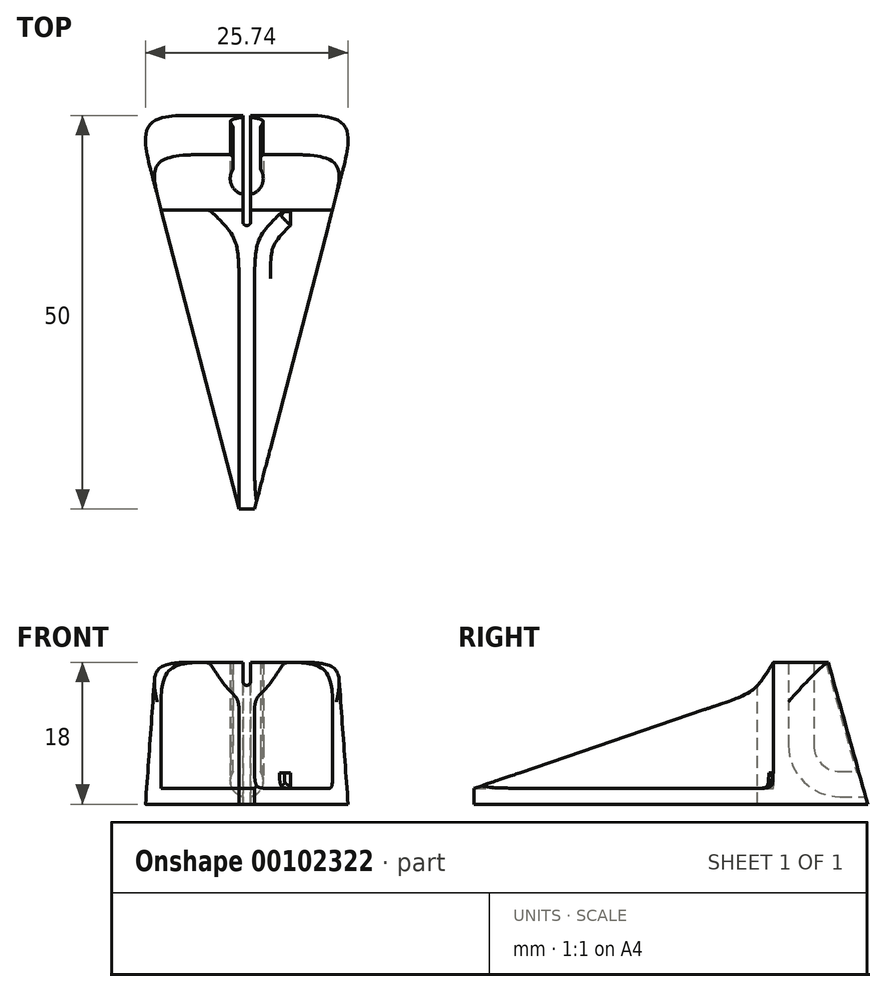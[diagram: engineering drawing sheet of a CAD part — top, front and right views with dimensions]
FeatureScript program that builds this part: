
annotation { "Feature Type Name" : "Feature", "Feature Type Description" : "" }
export const myFeature = defineFeature(function(context is Context, id is Id, definition is map)
    precondition{}
    {
        {
            var Q0;
            Q0=qCreatedBy(makeId("Top.planeOp"),FACE);
            var sketch = newSketch(context, id + "F0", { "sketchPlane" : qUnion([Q0])});
            skLineSegment(sketch, "E0", {"start": v(0, 0) * mm, "end": v(0, -42) * mm});
            skLineSegment(sketch, "E1", {"start": v(0, -42) * mm, "end": v(1, -42) * mm});
            skLineSegment(sketch, "E2", {"start": v(1, -42) * mm, "end": v(14, 8) * mm});
            skLineSegment(sketch, "E3", {"start": v(14, 8) * mm, "end": v(2, 8) * mm});
            skLineSegment(sketch, "E4", {"start": v(2, 8) * mm, "end": v(2, 0) * mm, "construction": true});
            skLineSegment(sketch, "E5", {"start": v(2, 0) * mm, "end": v(0, 0) * mm, "construction": true});
            skLineSegment(sketch, "E6", {"start": v(0, 0) * mm, "end": v(0, 8) * mm});
            skLineSegment(sketch, "E7", {"start": v(0, 8) * mm, "end": v(2, 8) * mm});
            skSolve(sketch);
        }
        {
            var Q0;
            Q0 = qSketchRegion(id + "F0", true);
            extrude(context, id + "F1", {"entities" : qUnion([Q0]), "depth" : 2 * mm});
        }
        {
            var Q0;
            Q0=makeQuery(id+"F1.opExtrude","SWEPT_BODY",BODY,{"disambiguationData":[OSD([sQuery(id+"F0.wireOp",EDGE,"E0"),sQuery(id+"F0.wireOp",EDGE,"E1"),sQuery(id+"F0.wireOp",EDGE,"E2"),sQuery(id+"F0.wireOp",EDGE,"E3"),sQuery(id+"F0.wireOp",EDGE,"E4"),sQuery(id+"F0.wireOp",EDGE,"E5")])]});
            var Q1;
            Q1=makeQuery(id+"F1.opExtrude","SWEPT_FACE",FACE,{"disambiguationData":[OSD([sQuery(id+"F0.wireOp",EDGE,"E0")])]});
            mirror(context, id + "F2", {"operationType" : NewBodyOperationType.ADD, "entities" : qUnion([Q0]), "mirrorPlane" : qUnion([Q1])});
        }
        {
            var Q0;
            {var subQ0=makeQuery(id+"F1.opExtrude","CAP_FACE",FACE,{"disambiguationData":[OSD([sQuery(id+"F0.wireOp",EDGE,"E0"),sQuery(id+"F0.wireOp",EDGE,"E1"),sQuery(id+"F0.wireOp",EDGE,"E2"),sQuery(id+"F0.wireOp",EDGE,"E3"),sQuery(id+"F0.wireOp",EDGE,"E6"),sQuery(id+"F0.wireOp",EDGE,"E7")])],"isStart":false});Q0=makeQuery(id+"F2.boolean.opBoolean","MERGE",FACE,{"derivedFrom":[subQ0,makeQuery(id+"F2.opPattern","COPY",FACE,{"derivedFrom":subQ0,"instanceName":"1"})]});}
            var sketch = newSketch(context, id + "F3", { "sketchPlane" : qUnion([Q0])});
            skLineSegment(sketch, "E8", {"start": v(0, 0) * mm, "end": v(1.75, 0) * mm});
            skLineSegment(sketch, "E9", {"start": v(1.75, 0) * mm, "end": v(1.75, 8) * mm});
            skLineSegment(sketch, "E10", {"start": v(1.75, 8) * mm, "end": v(4.75, 8) * mm});
            skLineSegment(sketch, "E11", {"start": v(-1, -6.17) * mm, "end": v(-4.75, -4) * mm});
            skLineSegment(sketch, "E12", {"start": v(-4.75, 8) * mm, "end": v(-1.75, 8) * mm});
            skLineSegment(sketch, "E13", {"start": v(-1.75, 8) * mm, "end": v(-1.75, 0) * mm});
            skLineSegment(sketch, "E14", {"start": v(-1.75, 0) * mm, "end": v(0, 0) * mm});
            skLineSegment(sketch, "E15", {"start": v(-4.75, -4) * mm, "end": v(4.75, -4) * mm, "construction": true});
            skLineSegment(sketch, "E16", {"start": v(-1, -6.17) * mm, "end": v(-1, -42) * mm});
            skLineSegment(sketch, "E17", {"start": v(-1, -42) * mm, "end": v(1, -42) * mm});
            skLineSegment(sketch, "E18", {"start": v(1, -42) * mm, "end": v(1, -6.17) * mm});
            skLineSegment(sketch, "E19", {"start": v(1, -6.17) * mm, "end": v(4.75, -4) * mm});
            skLineSegment(sketch, "E20", {"start": v(-4.75, -4) * mm, "end": v(-10.88, -4) * mm});
            skLineSegment(sketch, "E21", {"start": v(-10.88, -4) * mm, "end": v(-11.66, -1) * mm});
            skLineSegment(sketch, "E22", {"start": v(-11.66, -1) * mm, "end": v(-4.75, -1) * mm, "construction": true});
            skLineSegment(sketch, "E23", {"start": v(-4.75, -1) * mm, "end": v(-4.75, 8) * mm, "construction": true});
            skLineSegment(sketch, "E24", {"start": v(4.75, 8) * mm, "end": v(4.75, -1) * mm, "construction": true});
            skLineSegment(sketch, "E25", {"start": v(4.75, -1) * mm, "end": v(11.66, -1) * mm, "construction": true});
            skLineSegment(sketch, "E26", {"start": v(11.66, -1) * mm, "end": v(10.88, -4) * mm});
            skLineSegment(sketch, "E27", {"start": v(10.88, -4) * mm, "end": v(4.75, -4) * mm});
            skLineSegment(sketch, "E28", {"start": v(4.75, -1) * mm, "end": v(4.75, -4) * mm, "construction": true});
            skLineSegment(sketch, "E29", {"start": v(-4.75, -1) * mm, "end": v(-4.75, -4) * mm, "construction": true});
            skLineSegment(sketch, "E30", {"start": v(4.75, 8) * mm, "end": v(14, 8) * mm});
            skLineSegment(sketch, "E31", {"start": v(14, 8) * mm, "end": v(11.66, -1) * mm});
            skLineSegment(sketch, "E32", {"start": v(-4.75, 8) * mm, "end": v(-14, 8) * mm});
            skLineSegment(sketch, "E33", {"start": v(-14, 8) * mm, "end": v(-11.66, -1) * mm});
            skSolve(sketch);
        }
        {
            var Q0;
            Q0 = qSketchRegion(id + "F3", true);
            extrude(context, id + "F4", {"entities" : qUnion([Q0]), "operationType" : NewBodyOperationType.ADD, "depth" : 16 * mm});
        }
        {
            var Q0;
            Q0=qCreatedBy(makeId("Right.planeOp"),FACE);
            var sketch = newSketch(context, id + "F5", { "sketchPlane" : qUnion([Q0])});
            skLineSegment(sketch, "E34", {"start": v(8, 18) * mm, "end": v(8, 0) * mm});
            skLineSegment(sketch, "E35", {"start": v(8, 0) * mm, "end": v(3, 18) * mm});
            skLineSegment(sketch, "E36", {"start": v(3, 18) * mm, "end": v(8, 18) * mm});
            skSolve(sketch);
        }
        {
            var Q0;
            Q0 = qSketchRegion(id + "F5", true);
            extrude(context, id + "F6", {"entities" : qUnion([Q0]), "operationType" : NewBodyOperationType.REMOVE, "endBound" : BoundingType.THROUGH_ALL, "oppositeDirection" : true, "depth" : 25 * mm, "hasSecondDirection" : true, "secondDirectionBound" : SecondDirectionBoundingType.THROUGH_ALL, "secondDirectionOppositeDirection" : false, "secondDirectionDepth" : 25 * mm});
        }
        {
            var Q0;
            Q0=qCreatedBy(makeId("Right.planeOp"),FACE);
            var sketch = newSketch(context, id + "F7", { "sketchPlane" : qUnion([Q0])});
            skLineSegment(sketch, "E37", {"start": v(-4, 18) * mm, "end": v(-6.17, 14.25) * mm});
            skLineSegment(sketch, "E38", {"start": v(-6.17, 14.25) * mm, "end": v(-42, 2) * mm});
            skLineSegment(sketch, "E39", {"start": v(-42, 2) * mm, "end": v(-42, 18) * mm});
            skLineSegment(sketch, "E40", {"start": v(-42, 18) * mm, "end": v(-4, 18) * mm});
            skSolve(sketch);
        }
        {
            var Q0;
            Q0 = qSketchRegion(id + "F7", true);
            extrude(context, id + "F8", {"entities" : qUnion([Q0]), "operationType" : NewBodyOperationType.REMOVE, "endBound" : BoundingType.THROUGH_ALL, "oppositeDirection" : true, "depth" : 25 * mm, "hasSecondDirection" : true, "secondDirectionBound" : SecondDirectionBoundingType.THROUGH_ALL, "secondDirectionOppositeDirection" : false, "secondDirectionDepth" : 25 * mm});
        }
        {
            var Q0;
            Q0=makeQuery(id+"F4.opExtrude","SWEPT_EDGE",EDGE,{"disambiguationData":[OSD([sQuery(id+"F3.wireOp",EDGE,"E11"),sQuery(id+"F3.wireOp",EDGE,"E16")])]});
            var Q1;
            Q1=makeQuery(id+"F8.boolean.opBoolean","COPY",EDGE,{"derivedFrom":makeQuery(id+"F8.opExtrude","SWEPT_EDGE",EDGE,{"disambiguationData":[OSD([sQuery(id+"F7.wireOp",EDGE,"E37"),sQuery(id+"F7.wireOp",EDGE,"E38")])]})});
            var Q2;
            Q2=makeQuery(id+"F4.opExtrude","SWEPT_EDGE",EDGE,{"disambiguationData":[OSD([sQuery(id+"F3.wireOp",EDGE,"E18"),sQuery(id+"F3.wireOp",EDGE,"E19")])]});
            fillet(context, id + "F9", {"entities" : qUnion([Q0, Q1, Q2]), "radius" : 12 * mm, "tangentPropagation" : true, "rho" : 0.7, "crossSection" : FilletCrossSection.CONIC, "allowEdgeOverflow" : false});
        }
        {
            var Q0;
            Q0=makeQuery(id+"F4.opExtrude","CAP_EDGE",EDGE,{"disambiguationData":[OSD([sQuery(id+"F3.wireOp",EDGE,"E18")])],"isStart":true});
            var Q1;
            Q1=makeQuery(id+"F4.opExtrude","CAP_EDGE",EDGE,{"disambiguationData":[OSD([sQuery(id+"F3.wireOp",EDGE,"E16")])],"isStart":true});
            var Q2;
            Q2=makeQuery(id+"F9.opFillet","BLEND_EDGE",EDGE,{"blendedFrom":[makeQuery(id+"F4.opExtrude","SWEPT_EDGE",EDGE,{"disambiguationData":[OSD([sQuery(id+"F3.wireOp",EDGE,"E11"),sQuery(id+"F3.wireOp",EDGE,"E16")])]}),makeQuery(id+"F4.opExtrude","SWEPT_FACE",FACE,{"disambiguationData":[OSD([sQuery(id+"F3.wireOp",EDGE,"E20")])]})],"blendedInto":[makeQuery(id+"F4.opExtrude","SWEPT_FACE",FACE,{"disambiguationData":[OSD([sQuery(id+"F3.wireOp",EDGE,"E20")])]})]});
            var Q3;
            Q3=makeQuery(id+"F9.opFillet","BLEND_EDGE",EDGE,{"blendedFrom":[makeQuery(id+"F4.opExtrude","SWEPT_EDGE",EDGE,{"disambiguationData":[OSD([sQuery(id+"F3.wireOp",EDGE,"E18"),sQuery(id+"F3.wireOp",EDGE,"E19")])]}),makeQuery(id+"F4.opExtrude","SWEPT_FACE",FACE,{"disambiguationData":[OSD([sQuery(id+"F3.wireOp",EDGE,"E27")])]})],"blendedInto":[makeQuery(id+"F4.opExtrude","SWEPT_FACE",FACE,{"disambiguationData":[OSD([sQuery(id+"F3.wireOp",EDGE,"E27")])]})]});
            var Q4;
            Q4=makeQuery(id+"F4.opExtrude","SWEPT_EDGE",EDGE,{"disambiguationData":[OSD([sQuery(id+"F3.wireOp",EDGE,"E24"),sQuery(id+"F3.wireOp",EDGE,"E25")])]});
            var Q5;
            Q5=makeQuery(id+"F4.opExtrude","CAP_EDGE",EDGE,{"disambiguationData":[OSD([sQuery(id+"F3.wireOp",EDGE,"E24")])],"isStart":true});
            var Q6;
            Q6=makeQuery(id+"F4.opExtrude","CAP_EDGE",EDGE,{"disambiguationData":[OSD([sQuery(id+"F3.wireOp",EDGE,"E23")])],"isStart":true});
            var Q7;
            Q7=makeQuery(id+"F4.opExtrude","SWEPT_EDGE",EDGE,{"disambiguationData":[OSD([sQuery(id+"F3.wireOp",EDGE,"E22"),sQuery(id+"F3.wireOp",EDGE,"E23")])]});
            var Q8;
            Q8=makeQuery(id+"F4.opExtrude","CAP_EDGE",EDGE,{"disambiguationData":[OSD([sQuery(id+"F3.wireOp",EDGE,"E20")])],"isStart":true});
            var Q9;
            Q9=makeQuery(id+"F4.opExtrude","CAP_EDGE",EDGE,{"disambiguationData":[OSD([sQuery(id+"F3.wireOp",EDGE,"E27")])],"isStart":true});
            fillet(context, id + "F10", {"entities" : qUnion([Q0, Q1, Q2, Q3, Q4, Q5, Q6, Q7, Q8, Q9]), "radius" : 2 * mm, "tangentPropagation" : true, "rho" : .7, "crossSection" : FilletCrossSection.CONIC, "allowEdgeOverflow" : false});
        }
        {
            var Q0;
            Q0=makeQuery(id+"F6.boolean.opBoolean","INTERSECT",EDGE,{"derivedFrom":[makeQuery(id+"F2.opPattern","COPY",FACE,{"derivedFrom":makeQuery(id+"F1.opExtrude","SWEPT_FACE",FACE,{"disambiguationData":[OSD([sQuery(id+"F0.wireOp",EDGE,"E2")])]}),"instanceName":"1"}),makeQuery(id+"F6.opExtrude","SWEPT_FACE",FACE,{"disambiguationData":[OSD([sQuery(id+"F5.wireOp",EDGE,"E35")])]})]});
            var Q1;
            Q1=makeQuery(id+"F6.boolean.opBoolean","INTERSECT",EDGE,{"derivedFrom":[makeQuery(id+"F1.opExtrude","SWEPT_FACE",FACE,{"disambiguationData":[OSD([sQuery(id+"F0.wireOp",EDGE,"E2")])]}),makeQuery(id+"F6.opExtrude","SWEPT_FACE",FACE,{"disambiguationData":[OSD([sQuery(id+"F5.wireOp",EDGE,"E35")])]})]});
            var Q2;
            Q2=makeQuery(id+"F4.opExtrude","CAP_EDGE",EDGE,{"disambiguationData":[OSD([sQuery(id+"F3.wireOp",EDGE,"E26")])],"isStart":false});
            var Q3;
            Q3=makeQuery(id+"F4.opExtrude","CAP_EDGE",EDGE,{"disambiguationData":[OSD([sQuery(id+"F3.wireOp",EDGE,"E21")])],"isStart":false});
            fillet(context, id + "F11", {"entities" : qUnion([Q0, Q1, Q2, Q3]), "radius" : 5 * mm, "tangentPropagation" : true, "rho" : .6, "crossSection" : FilletCrossSection.CONIC, "allowEdgeOverflow" : false});
        }
        {
            var Q0;
            Q0=qCreatedBy(makeId("Front.planeOp"),FACE);
            var sketch = newSketch(context, id + "F12", { "sketchPlane" : qUnion([Q0])});
            skCircle(sketch, "E41", {"center": v(0, 2.97) * mm, "radius": 2 * mm});
            skSolve(sketch);
        }
        {
            var Q0;
            Q0=qCreatedBy(makeId("Right.planeOp"),FACE);
            var sketch = newSketch(context, id + "F13", { "sketchPlane" : qUnion([Q0])});
            skLineSegment(sketch, "E42", {"start": v(9.7, 2.97) * mm, "end": v(4.5, 2.97) * mm});
            skLineSegment(sketch, "E43", {"start": v(0, 7.47) * mm, "end": v(0, 18) * mm});
            skPoint(sketch, "E44.visualSharp", {"position": v(0, 2.97) * mm});
            skArc(sketch, "E44.filletArc", {"start": v(0, 7.47) * mm, "mid": v(1.32, 4.29) * mm, "end": v(4.5, 2.97) * mm});
            skSolve(sketch);
        }
        {
            var Q0;
            Q0=makeQuery(id+"F4.opExtrude","CAP_FACE",FACE,{"disambiguationData":[OSD([sQuery(id+"F3.wireOp",EDGE,"E8"),sQuery(id+"F3.wireOp",EDGE,"E9"),sQuery(id+"F3.wireOp",EDGE,"E10"),sQuery(id+"F3.wireOp",EDGE,"5PolXJmB-3XB9-REXe-LaWg-8huEXrEMtkN5"),sQuery(id+"F3.wireOp",EDGE,"E11"),sQuery(id+"F3.wireOp",EDGE,"3jHEL8MU-E7O7-Db6z-O08p-L8hBiCzpWRcO"),sQuery(id+"F3.wireOp",EDGE,"E12"),sQuery(id+"F3.wireOp",EDGE,"E13"),sQuery(id+"F3.wireOp",EDGE,"E14"),sQuery(id+"F3.wireOp",EDGE,"E16"),sQuery(id+"F3.wireOp",EDGE,"E17"),sQuery(id+"F3.wireOp",EDGE,"E18"),sQuery(id+"F3.wireOp",EDGE,"E19")])],"isStart":false});
            var sketch = newSketch(context, id + "F14", { "sketchPlane" : qUnion([Q0])});
            skCircle(sketch, "E45", {"center": v(0, 0) * mm, "radius": 2.1 * mm});
            skSolve(sketch);
        }
        {
            var Q0;
            Q0=makeQuery(id+"F4.opExtrude","CAP_EDGE",EDGE,{"disambiguationData":[OSD([sQuery(id+"F3.wireOp",EDGE,"E8"),sQuery(id+"F3.wireOp",EDGE,"E14")])],"isStart":true});
            chamfer(context, id + "F15", {"entities" : qUnion([Q0]), "width" : 4 * mm, "tangentPropagation" : true});
        }
        {
            var Q0;
            Q0 = qSketchRegion(id + "F14", true);
            var Q1;
            Q1 = qConstructionFilter(qBodyType(qCreatedBy(id + "F13" ,EDGE), BodyType.WIRE), ConstructionObject.NO);
            sweep(context, id + "F16", {"operationType" : NewBodyOperationType.REMOVE, "profiles" : qUnion([Q0]), "path" : qUnion([Q1])});
        }
        {
            var Q0;
            Q0=makeQuery(id+"F4.opExtrude","CAP_FACE",FACE,{"disambiguationData":[OSD([sQuery(id+"F3.wireOp",EDGE,"E8"),sQuery(id+"F3.wireOp",EDGE,"E9"),sQuery(id+"F3.wireOp",EDGE,"E10"),sQuery(id+"F3.wireOp",EDGE,"5PolXJmB-3XB9-REXe-LaWg-8huEXrEMtkN5"),sQuery(id+"F3.wireOp",EDGE,"E11"),sQuery(id+"F3.wireOp",EDGE,"3jHEL8MU-E7O7-Db6z-O08p-L8hBiCzpWRcO"),sQuery(id+"F3.wireOp",EDGE,"E12"),sQuery(id+"F3.wireOp",EDGE,"E13"),sQuery(id+"F3.wireOp",EDGE,"E14"),sQuery(id+"F3.wireOp",EDGE,"E16"),sQuery(id+"F3.wireOp",EDGE,"E17"),sQuery(id+"F3.wireOp",EDGE,"E18"),sQuery(id+"F3.wireOp",EDGE,"E19")])],"isStart":false});
            var sketch = newSketch(context, id + "F17", { "sketchPlane" : qUnion([Q0])});
            skLineSegment(sketch, "E46.bottom", {"start": v(-0.5, -6) * mm, "end": v(0.5, -6) * mm});
            skLineSegment(sketch, "E46.top", {"start": v(-0.5, 8) * mm, "end": v(0.5, 8) * mm});
            skLineSegment(sketch, "E46.left", {"start": v(-0.5, -6) * mm, "end": v(-0.5, 8) * mm});
            skLineSegment(sketch, "E46.right", {"start": v(0.5, -6) * mm, "end": v(0.5, 8) * mm});
            skLineSegment(sketch, "E47", {"start": v(0, -6) * mm, "end": v(0, 0) * mm, "construction": true});
            skLineSegment(sketch, "E48", {"start": v(0, -4) * mm, "end": v(0, -6) * mm, "construction": true});
            skSolve(sketch);
        }
        {
            var Q0;
            Q0 = qSketchRegion(id + "F17", true);
            extrude(context, id + "F18", {"entities" : qUnion([Q0]), "operationType" : NewBodyOperationType.REMOVE, "endBound" : BoundingType.THROUGH_ALL, "oppositeDirection" : true, "depth" : 25 * mm});
        }
        {
            var Q0;
            Q0=makeQuery(id+"F18.boolean.opBoolean","COPY",EDGE,{"derivedFrom":makeQuery(id+"F18.opExtrude","SWEPT_EDGE",EDGE,{"disambiguationData":[OSD([sQuery(id+"F17.wireOp",EDGE,"E46.bottom"),sQuery(id+"F17.wireOp",EDGE,"E46.left")])]})});
            var Q1;
            Q1=makeQuery(id+"F18.boolean.opBoolean","COPY",EDGE,{"derivedFrom":makeQuery(id+"F18.opExtrude","SWEPT_EDGE",EDGE,{"disambiguationData":[OSD([sQuery(id+"F17.wireOp",EDGE,"E46.bottom"),sQuery(id+"F17.wireOp",EDGE,"E46.right")])]})});
            fillet(context, id + "F19", {"entities" : qUnion([Q0, Q1]), "radius" : .5 * mm, "tangentPropagation" : true, "allowEdgeOverflow" : false});
        }
        {
            var Q0;
            Q0=makeQuery(id+"F6.boolean.opBoolean","INTERSECT",EDGE,{"derivedFrom":[makeQuery(id+"F4.opExtrude","SWEPT_FACE",FACE,{"disambiguationData":[OSD([sQuery(id+"F3.wireOp",EDGE,"E13")])]}),makeQuery(id+"F6.opExtrude","SWEPT_FACE",FACE,{"disambiguationData":[OSD([sQuery(id+"F5.wireOp",EDGE,"E35")])]})]});
            var Q1;
            Q1=makeQuery(id+"F6.boolean.opBoolean","INTERSECT",EDGE,{"derivedFrom":[makeQuery(id+"F4.opExtrude","SWEPT_FACE",FACE,{"disambiguationData":[OSD([sQuery(id+"F3.wireOp",EDGE,"E9")])]}),makeQuery(id+"F6.opExtrude","SWEPT_FACE",FACE,{"disambiguationData":[OSD([sQuery(id+"F5.wireOp",EDGE,"E35")])]})]});
            chamfer(context, id + "F20", {"entities" : qUnion([Q0, Q1]), "width" : .3 * mm, "tangentPropagation" : true});
        }
    });
